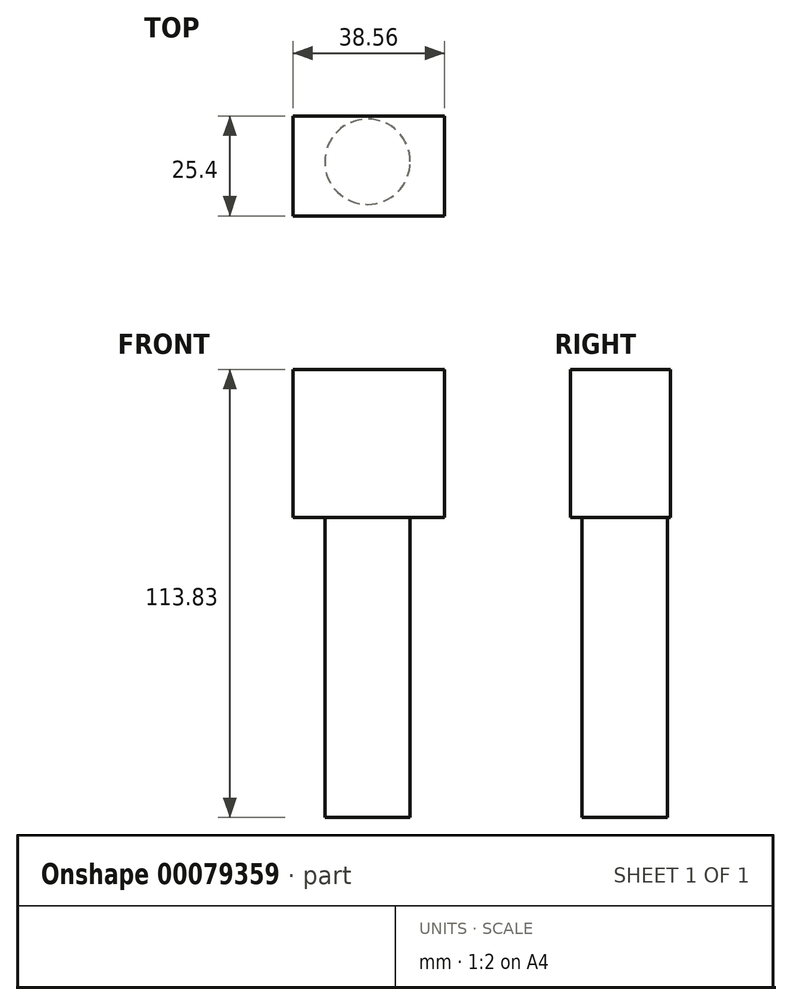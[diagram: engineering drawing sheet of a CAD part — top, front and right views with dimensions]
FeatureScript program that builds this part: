
annotation { "Feature Type Name" : "Feature", "Feature Type Description" : "" }
export const myFeature = defineFeature(function(context is Context, id is Id, definition is map)
    precondition{}
    {
        {
            var Q0;
            Q0=qCreatedBy(makeId("Front.planeOp"),FACE);
            var sketch = newSketch(context, id + "F0", { "sketchPlane" : qUnion([Q0])});
            skLineSegment(sketch, "E0.bottom", {"start": v(-48.03, 19.66) * mm, "end": v(-9.47, 19.66) * mm});
            skLineSegment(sketch, "E0.top", {"start": v(-48.03, -17.97) * mm, "end": v(-9.47, -17.97) * mm});
            skLineSegment(sketch, "E0.left", {"start": v(-48.03, 19.66) * mm, "end": v(-48.03, -17.97) * mm});
            skLineSegment(sketch, "E0.right", {"start": v(-9.47, 19.66) * mm, "end": v(-9.47, -17.97) * mm});
            skSolve(sketch);
        }
        {
            var Q0;
            Q0 = qSketchRegion(id + "F0", true);
            extrude(context, id + "F1", {"entities" : qUnion([Q0]), "depth" : 25.4 * mm});
        }
        {
            var Q0;
            Q0=makeQuery(id+"F1.opExtrude","SWEPT_FACE",FACE,{"disambiguationData":[OSD([sQuery(id+"F0.wireOp",EDGE,"E0.top")])]});
            var sketch = newSketch(context, id + "F2", { "sketchPlane" : qUnion([Q0])});
            skCircle(sketch, "E1", {"center": v(-29.07, 11.62) * mm, "radius": 10.85 * mm});
            skSolve(sketch);
        }
        {
            var Q0;
            Q0 = qSketchRegion(id + "F2", true);
            extrude(context, id + "F3", {"entities" : qUnion([Q0]), "operationType" : NewBodyOperationType.ADD, "depth" : 76.2 * mm});
        }
    });
